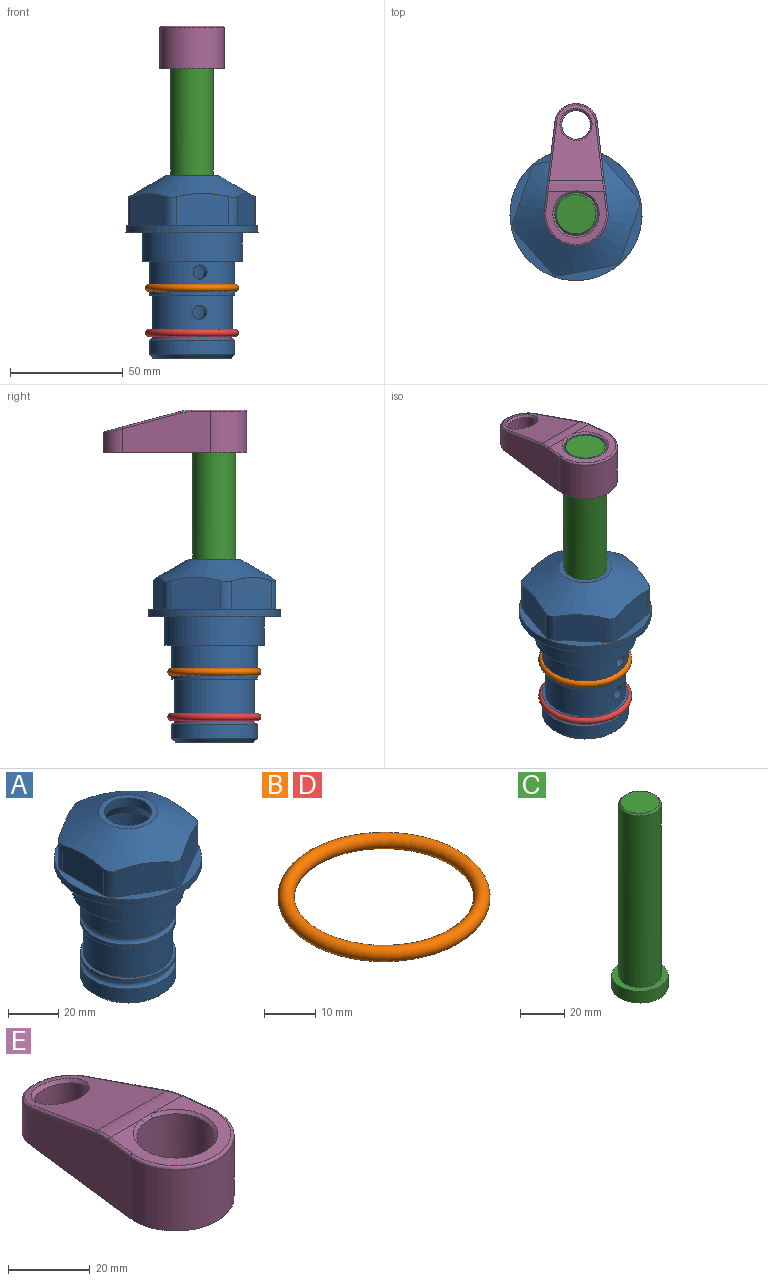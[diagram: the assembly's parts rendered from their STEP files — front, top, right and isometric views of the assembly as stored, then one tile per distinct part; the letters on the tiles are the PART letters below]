
ASSEMBLY  parts=5 mates=4
PART A: 36 faces, bbox 58.7x58.7x81 mm
  f0: cylinder r=17.78mm len=35.56mm, axis (0,0,1), area 1670.8mm2, adj f23,f24,f31
  f1: cylinder r=19.05mm len=38.1mm, axis (0,0,1), area 1191.9mm2, adj f26,f27,f30
  f2: plane 58.66x58.66mm, normal (0,0,-1), area 1150.6mm2, adj f3,f28
  f3: cylinder r=29.33mm len=58.66mm, axis (0,0,-1), area 585.1mm2, adj f2,f4
  f4: plane 58.66x58.66mm, normal (0,0,1), area 475.9mm2, adj f3,f5,f6,f7,f8,f9,f10,f11
  f5: plane 20.32x14.34mm, normal (-0.5,0.87,0), area 324.4mm2, adj f4,f15,f16,f17
  f6: plane 20.32x14.34mm, normal (0.5,0.87,0), area 324.4mm2, adj f4,f14,f15,f17
  f7: plane 23.48x14.34mm, normal (1,0,0), area 324.4mm2, adj f4,f13,f14,f17
  f8: plane 20.32x14.34mm, normal (0.5,-0.87,0), area 324.4mm2, adj f4,f12,f13,f17
  f9: plane 20.32x14.34mm, normal (-0.5,-0.87,0), area 324.4mm2, adj f4,f11,f12,f17
  f10: plane 23.48x14.34mm, normal (-1,0,0), area 324.4mm2, adj f4,f11,f16,f17
  f11: cylinder r=5.08mm len=12.85mm, axis (0,0,-1), area 67.2mm2, adj f4,f9,f10,f17
  f12: cylinder r=5.08mm len=12.85mm, axis (0,0,-1), area 67.2mm2, adj f4,f8,f9,f17
  f13: cylinder r=5.08mm len=12.85mm, axis (0,0,-1), area 67.2mm2, adj f4,f7,f8,f17
  f14: cylinder r=5.08mm len=12.85mm, axis (0,0,-1), area 67.2mm2, adj f4,f6,f7,f17
  f15: cylinder r=5.08mm len=12.85mm, axis (0,0,-1), area 67.2mm2, adj f4,f5,f6,f17
  f16: cylinder r=5.08mm len=12.85mm, axis (0,0,-1), area 67.2mm2, adj f4,f5,f10,f17
  f17: cone r=11.73mm half-angle=60deg, axis (0,0,-1), area 2071.8mm2, adj f5,f6,f7,f8,f9,f10,f11,f12
  f18: plane 23.46x23.46mm, normal (0,0,1), area 147.4mm2, adj f17,f35
  f19: plane 34.93x34.93mm, normal (0,0,-1), area 958mm2, adj f29
  f20: cylinder r=19.05mm len=38.1mm, axis (0,0,1), area 760.1mm2, adj f21,f29
  f21: torus R=19.05mm, axis (0,0,1), area 565.3mm2, adj f20,f22
  f22: cylinder r=19.05mm len=38.1mm, axis (0,0,1), area 190mm2, adj f21,f23
  f23: plane 38.1x38.1mm, normal (0,0,1), area 146.9mm2, adj f0,f22
  f24: plane 38.1x38.1mm, normal (0,0,-1), area 146.9mm2, adj f0,f25
  f25: cylinder r=19.05mm len=38.1mm, axis (0,0,1), area 190mm2, adj f24,f26
  f26: torus R=19.05mm, axis (0,0,1), area 565.3mm2, adj f1,f25
  f27: plane 44.45x44.45mm, normal (0,0,-1), area 411.7mm2, adj f1,f28
  f28: cylinder r=22.23mm len=44.45mm, axis (0,0,1), area 1773.5mm2, adj f2,f27
  f29: cone r=19.05mm half-angle=45deg, axis (0,0,1), area 257.5mm2, adj f19,f20
  f30: cylinder r=3.17mm len=6.75mm, axis (-1,0,0), area 128mm2, adj f1,f33
  f31: cylinder r=3.17mm len=6.35mm, axis (-1,0,0), area 102.5mm2, adj f0,f33
  f32: plane 25.4x25.4mm, normal (0,0,1), area 506.7mm2, adj f33
  f33: cylinder r=12.7mm len=66.42mm, axis (0,0,-1), area 5236.2mm2, adj f30,f31,f32,f34
  f34: cone r=9.53mm half-angle=30deg, axis (0,0,-1), area 443.4mm2, adj f33,f35
  f35: cylinder r=9.53mm len=19.05mm, axis (0,0,-1), area 240.9mm2, adj f18,f34
PART B: 1 faces, bbox 44.7x44.7x3.2 mm
  f0: torus R=19.05mm, axis (0,0,1), area 1193.9mm2
PART C: 6 faces, bbox 25.4x25.4x101.6 mm
  f0: plane 17.46x17.46mm, normal (0,0,1), area 239.5mm2, adj f5
  f1: plane 25.4x25.4mm, normal (0,0,-1), area 506.7mm2, adj f2
  f2: cylinder r=12.7mm len=25.4mm, axis (0,0,1), area 506.7mm2, adj f1,f3
  f3: plane 25.4x25.4mm, normal (0,0,1), area 221.7mm2, adj f2,f4
  f4: cylinder r=9.53mm len=94.46mm, axis (0,0,1), area 5653mm2, adj f3,f5
  f5: cone r=8.73mm half-angle=45deg, axis (0,0,-1), area 64.4mm2, adj f0,f4
PART D: same geometry as B
PART E: 31 faces, bbox 31.7x65.5x19.8 mm
  f0: plane 39.12x18.26mm, normal (0.99,0.12,0), area 612.2mm2, adj f1,f4,f7,f11,f13,f15
  f1: cylinder r=9.53mm len=18.91mm, axis (0,0,-1), area 296.1mm2, adj f0,f2,f7,f17
  f2: plane 39.12x18.26mm, normal (-0.99,0.12,0), area 612.2mm2, adj f1,f4,f7,f12,f14,f16
  f3: cylinder r=6.35mm len=12.7mm, axis (0,0,-1), area 362.4mm2, adj f7,f18
  f4: cylinder r=14.29mm len=28.58mm, axis (0,0,-1), area 882.2mm2, adj f0,f2,f7,f10
  f5: cylinder r=9.53mm len=19.05mm, axis (0,0,-1), area 1092.6mm2, adj f7,f19,f20
  f6: plane 26.99x23.69mm, normal (0,0,1), area 216.2mm2, adj f9,f10,f11,f12,f19
  f7: plane 63.5x28.58mm, normal (0,0,-1), area 661.8mm2, adj f0,f1,f2,f3,f4,f5,f22,f23
  f8: plane 33.52x23.6mm, normal (0,0.26,0.97), area 486mm2, adj f9,f15,f16,f17,f18
  f9: cylinder r=19.05mm len=24.72mm, axis (1,0,0), area 120.4mm2, adj f6,f8,f13,f14,f20
  f10: torus R=13.49mm, axis (0,0,1), area 59mm2, adj f4,f6,f11,f12
  f11: cylinder r=0.79mm len=8.67mm, axis (0.12,-0.99,0), area 10.8mm2, adj f0,f6,f10,f13
  f12: cylinder r=0.79mm len=8.67mm, axis (0.12,0.99,0), area 10.8mm2, adj f2,f6,f10,f14
  f13: bspline ~4.95x1.42mm, area 6.1mm2, adj f0,f9,f11,f15
  f14: bspline ~4.95x1.42mm, area 6.1mm2, adj f2,f9,f12,f16
  f15: cylinder r=0.79mm len=25.95mm, axis (0.12,-0.96,0.26), area 32.9mm2, adj f0,f8,f13,f17
  f16: cylinder r=0.79mm len=25.95mm, axis (0.12,0.96,-0.26), area 32.9mm2, adj f2,f8,f14,f17
  f17: bspline ~18.91x8.38mm, area 30mm2, adj f1,f8,f15,f16
  f18: bspline ~14.29x14.29mm, area 48.3mm2, adj f3,f8
  f19: cone r=9.53mm half-angle=45deg, axis (0,0,1), area 66.5mm2, adj f5,f6,f20
  f20: bspline ~3.22x0.96mm, area 3.5mm2, adj f5,f9,f19
  f21: plane 2.75x2.72mm, normal (0,0,-1), area 2.9mm2, adj f23,f25,f28
  f22: plane 23.05x15.88mm, normal (-0.99,-0.12,0), area 323.6mm2, adj f7,f25,f26,f27,f28,f29
  f23: plane 23.05x15.88mm, normal (0.99,-0.12,0), area 323.6mm2, adj f7,f21,f25,f27,f28,f30
  f24: cylinder r=9.53mm len=10.69mm, axis (0,0,-1), area 114.7mm2, adj f7,f27,f29,f30
  f25: cylinder r=12.7mm len=20.59mm, axis (0,0,-1), area 381.1mm2, adj f7,f21,f22,f23,f26,f28
  f26: plane 2.75x2.72mm, normal (0,0,-1), area 2.9mm2, adj f22,f25,f28
  f27: plane 19.72x18.37mm, normal (0,-0.26,-0.97), area 291.8mm2, adj f22,f23,f24,f28,f29,f30
  f28: cylinder r=15.88mm len=19.92mm, axis (1,0,0), area 54.8mm2, adj f21,f22,f23,f25,f26,f27
  f29: cylinder r=1.59mm len=11mm, axis (0,0,-1), area 34.7mm2, adj f7,f22,f24,f27
  f30: cylinder r=1.59mm len=11mm, axis (0,0,-1), area 34.7mm2, adj f7,f23,f24,f27
PLACE A rot(axis=(0,0,-1),79.1deg) t=(0,0,-27.55)mm
PLACE B rot(axis=(0,0,-1),79.1deg) t=(0,0,-27.55)mm
PLACE C at identity fixed
PLACE D rot(axis=(0,0,-1),79.1deg) t=(0,0,-47.56)mm
PLACE E t=(0,0,0.79)mm
MATE fastened E.f4 <-> C.f2  axis (0,0,1) through (0,0,63.5)mm
MATE fastened D.f0 <-> A.f0  axis (0,0,1) through (0,0,-72.07)mm
MATE cylindrical A.f0 <-> C.f2  axis (0,0,1) through (0,0,-78.1)mm
MATE fastened B.f0 <-> A.f0  axis (0,0,1) through (0,0,-52.06)mm
